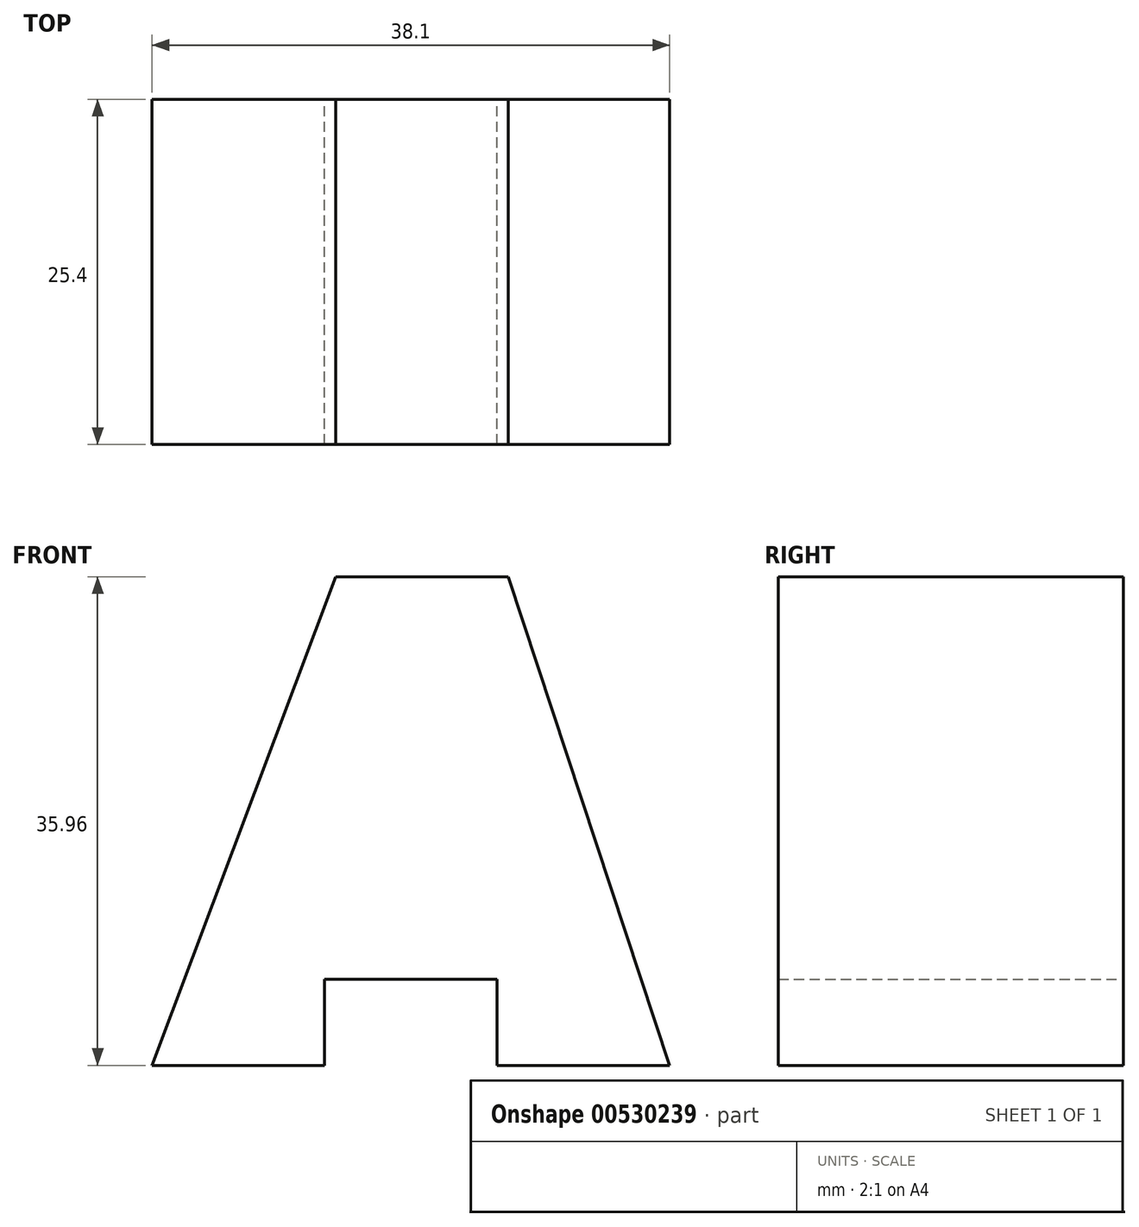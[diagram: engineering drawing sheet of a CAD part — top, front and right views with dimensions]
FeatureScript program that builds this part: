
annotation { "Feature Type Name" : "Feature", "Feature Type Description" : "" }
export const myFeature = defineFeature(function(context is Context, id is Id, definition is map)
    precondition{}
    {
        {
            var Q0;
            Q0=qCreatedBy(makeId("Front.planeOp"),FACE);
            var sketch = newSketch(context, id + "F0", { "sketchPlane" : qUnion([Q0])});
            skLineSegment(sketch, "E0", {"start": v(-64, 0) * mm, "end": v(-50.47, 35.96) * mm});
            skLineSegment(sketch, "E1", {"start": v(-50.47, 35.96) * mm, "end": v(-37.77, 35.96) * mm});
            skLineSegment(sketch, "E2", {"start": v(-37.77, 35.96) * mm, "end": v(-25.9, 0) * mm});
            skLineSegment(sketch, "E3", {"start": v(-25.9, 0) * mm, "end": v(-38.6, 0) * mm});
            skLineSegment(sketch, "E4", {"start": v(-38.6, 0) * mm, "end": v(-38.6, 6.35) * mm});
            skLineSegment(sketch, "E5", {"start": v(-38.6, 6.35) * mm, "end": v(-51.3, 6.35) * mm});
            skLineSegment(sketch, "E6", {"start": v(-51.3, 6.35) * mm, "end": v(-51.3, 0) * mm});
            skLineSegment(sketch, "E7", {"start": v(-51.3, 0) * mm, "end": v(-64, 0) * mm});
            skSolve(sketch);
        }
        {
            var Q0;
            Q0 = qSketchRegion(id + "F0", true);
            extrude(context, id + "F1", {"entities" : qUnion([Q0]), "depth" : 25.4 * mm, "offsetDistance" : 25.4 * mm});
        }
    });
